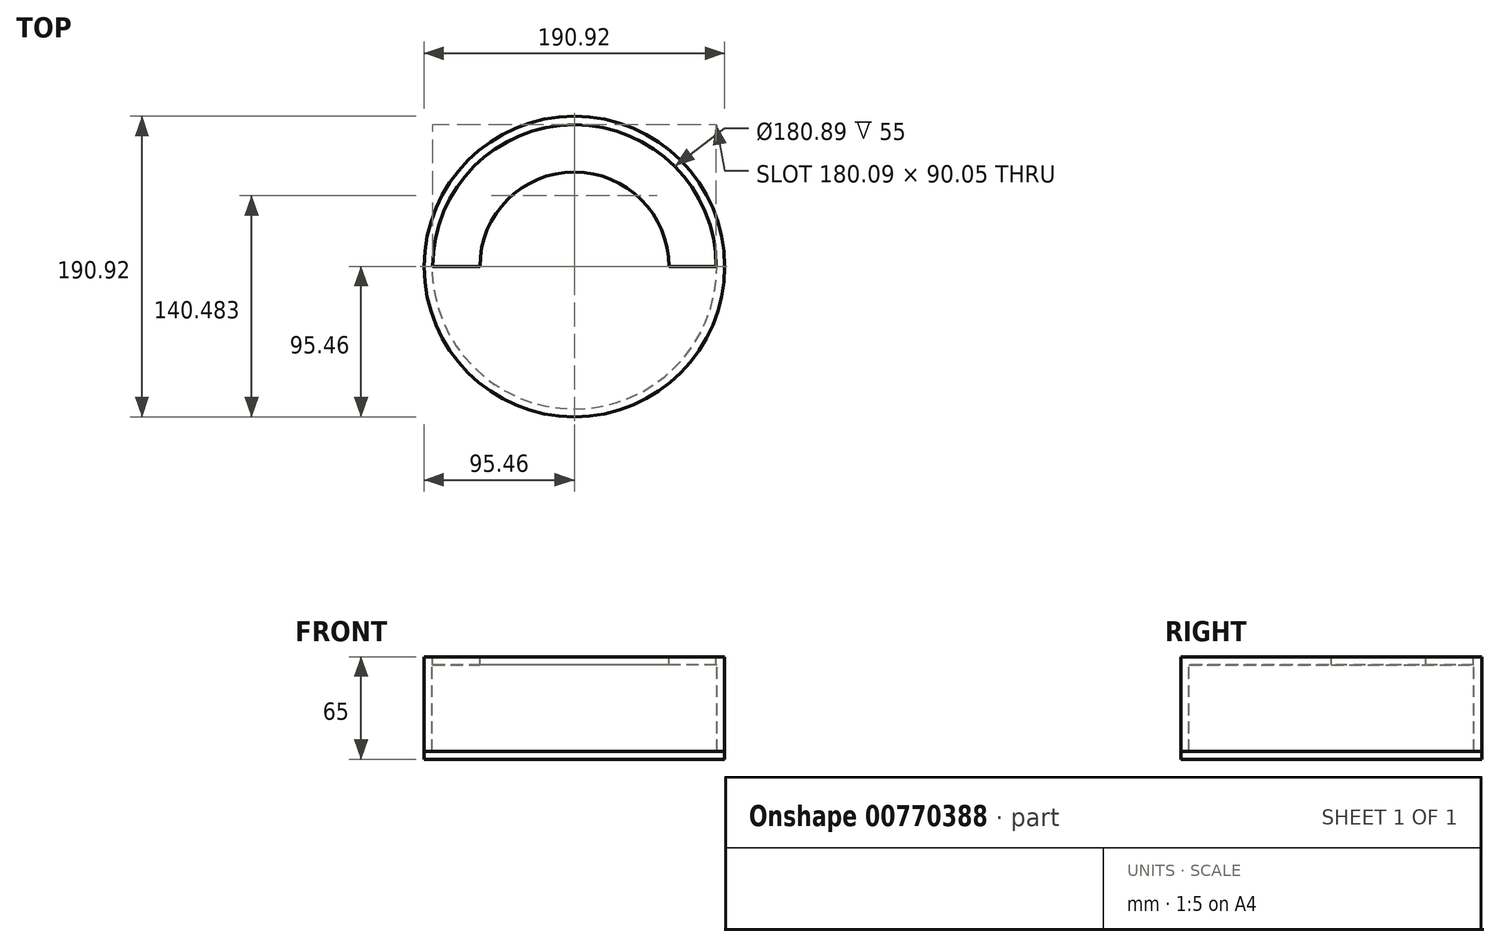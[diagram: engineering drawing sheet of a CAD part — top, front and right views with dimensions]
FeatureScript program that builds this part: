
annotation { "Feature Type Name" : "Feature", "Feature Type Description" : "" }
export const myFeature = defineFeature(function(context is Context, id is Id, definition is map)
    precondition{}
    {
        {
            var Q0;
            Q0=qCreatedBy(makeId("Top.planeOp"),FACE);
            var sketch = newSketch(context, id + "F0", { "sketchPlane" : qUnion([Q0])});
            skCircle(sketch, "E0", {"center": v(0, 0) * mm, "radius": 95.44 * mm});
            skSolve(sketch);
        }
        {
            var Q0;
            Q0 = qSketchRegion(id + "F0", true);
            extrude(context, id + "F1", {"entities" : qUnion([Q0]), "depth" : 60 * mm, "offsetDistance" : 25 * mm});
        }
        {
            var Q0;
            Q0=qCreatedBy(makeId("Top.planeOp"),FACE);
            cPlane(context, id + "F2", {"entities" : qUnion([Q0]), "cplaneType" : CPlaneType.OFFSET, "offset" : 60 * mm, "width" : 150 * mm, "height" : 150 * mm});
        }
        {
            var Q0;
            Q0=qCreatedBy(id+"F2.planeOp",FACE);
            var sketch = newSketch(context, id + "F3", { "sketchPlane" : qUnion([Q0])});
            skCircle(sketch, "E1", {"center": v(0, 0) * mm, "radius": 90.44 * mm});
            skSolve(sketch);
        }
        {
            var Q0;
            Q0=makeQuery(id+"F3.imprint","IMPRINT",FACE,{"disambiguationData":[TD([[makeQuery(id+"F3.imprint","IMPRINT",EDGE,{"derivedFrom":sQuery(id+"F3.wireOp",EDGE,"E1")}),1.0]])]});
            extrude(context, id + "F4", {"entities" : qUnion([Q0]), "operationType" : NewBodyOperationType.REMOVE, "oppositeDirection" : true, "depth" : 147 * mm, "offsetDistance" : 25 * mm});
        }
        {
            var Q0;
            Q0=qCreatedBy(id+"F2.planeOp",FACE);
            var sketch = newSketch(context, id + "F5", { "sketchPlane" : qUnion([Q0])});
            skCircle(sketch, "E2", {"center": v(0, 0) * mm, "radius": 95.44 * mm});
            skSolve(sketch);
        }
        {
            var Q0;
            Q0 = qSketchRegion(id + "F5", true);
            extrude(context, id + "F6", {"entities" : qUnion([Q0]), "operationType" : NewBodyOperationType.ADD, "depth" : 5 * mm, "offsetDistance" : 25 * mm});
        }
        {
            var Q0;
            Q0=qCreatedBy(makeId("Top.planeOp"),FACE);
            var sketch = newSketch(context, id + "F7", { "sketchPlane" : qUnion([Q0])});
            skCircle(sketch, "E3", {"center": v(0, 0) * mm, "radius": 95.46 * mm});
            skSolve(sketch);
        }
        {
            var Q0;
            Q0 = qSketchRegion(id + "F7", true);
            extrude(context, id + "F8", {"entities" : qUnion([Q0]), "operationType" : NewBodyOperationType.ADD, "depth" : 5 * mm, "offsetDistance" : 25 * mm});
        }
        {
            var Q0;
            Q0=qCreatedBy(id+"F2.planeOp",FACE);
            cPlane(context, id + "F9", {"entities" : qUnion([Q0]), "cplaneType" : CPlaneType.OFFSET, "offset" : 5 * mm, "width" : 150 * mm, "height" : 150 * mm});
        }
        {
            var Q0;
            Q0=qCreatedBy(id+"F9.planeOp",FACE);
            var sketch = newSketch(context, id + "F10", { "sketchPlane" : qUnion([Q0])});
            skArc(sketch, "E4", {"start": v(-90.05, 0) * mm, "mid": v(0, 90.05) * mm, "end": v(90.05, 0) * mm});
            skLineSegment(sketch, "E5", {"start": v(-90.05, 0) * mm, "end": v(-60.05, 0) * mm});
            skLineSegment(sketch, "E6", {"start": v(90.05, 0) * mm, "end": v(60.05, 0) * mm});
            skArc(sketch, "E7", {"start": v(-60.05, 0) * mm, "mid": v(0, 60.05) * mm, "end": v(60.05, 0) * mm});
            skSolve(sketch);
        }
        {
            var Q0;
            Q0 = qSketchRegion(id + "F10", true);
            extrude(context, id + "F11", {"entities" : qUnion([Q0]), "operationType" : NewBodyOperationType.REMOVE, "oppositeDirection" : true, "depth" : 25 * mm, "offsetDistance" : 25 * mm});
        }
    });
